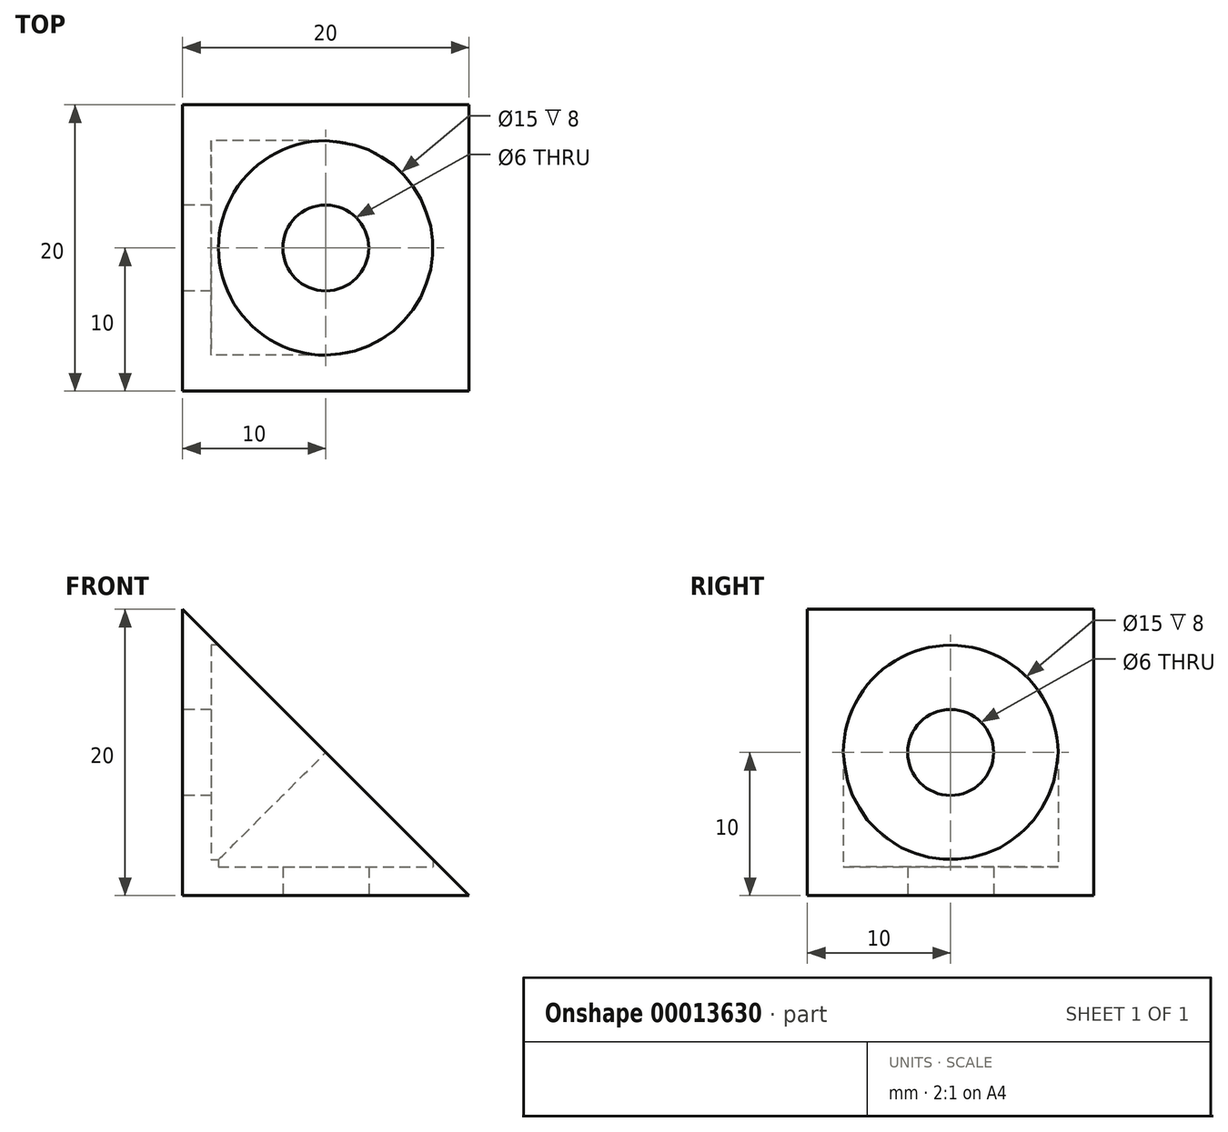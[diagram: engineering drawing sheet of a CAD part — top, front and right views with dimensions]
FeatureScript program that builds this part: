
annotation { "Feature Type Name" : "Feature", "Feature Type Description" : "" }
export const myFeature = defineFeature(function(context is Context, id is Id, definition is map)
    precondition{}
    {
        {
            var Q0;
            Q0=qCreatedBy(makeId("Front.planeOp"),FACE);
            var sketch = newSketch(context, id + "F0", { "sketchPlane" : qUnion([Q0])});
            skLineSegment(sketch, "E0", {"start": v(0, 0) * mm, "end": v(0, 20) * mm});
            skLineSegment(sketch, "E1", {"start": v(0, 0) * mm, "end": v(20, 0) * mm});
            skLineSegment(sketch, "E2", {"start": v(0, 20) * mm, "end": v(20, 0) * mm});
            skSolve(sketch);
        }
        {
            var Q0;
            Q0=makeQuery(id+"F0.imprint","IMPRINT",FACE,{"disambiguationData":[TD([[makeQuery(id+"F0.imprint","IMPRINT",EDGE,{"derivedFrom":sQuery(id+"F0.wireOp",EDGE,"E0")}),-1.0]])]});
            extrude(context, id + "F1", {"entities" : qUnion([Q0]), "depth" : 20 * mm});
        }
        {
            var Q0;
            Q0=makeQuery(id+"F1.opExtrude","SWEPT_FACE",FACE,{"disambiguationData":[OSD([sQuery(id+"F0.wireOp",EDGE,"E0")])]});
            var sketch = newSketch(context, id + "F2", { "sketchPlane" : qUnion([Q0])});
            skLineSegment(sketch, "E3", {"start": v(10, 0) * mm, "end": v(10, 20) * mm, "construction": true});
            skCircle(sketch, "E4", {"center": v(10, 10) * mm, "radius": 3 * mm});
            skCircle(sketch, "E5", {"center": v(10, 10) * mm, "radius": 7.5 * mm});
            skSolve(sketch);
        }
        {
            var Q0;
            Q0=makeQuery(id+"F2.imprint","IMPRINT",FACE,{"disambiguationData":[TD([[makeQuery(id+"F2.imprint","IMPRINT",EDGE,{"derivedFrom":sQuery(id+"F2.wireOp",EDGE,"E4")}),-1.0]])]});
            extrude(context, id + "F3", {"entities" : qUnion([Q0]), "operationType" : NewBodyOperationType.REMOVE, "oppositeDirection" : true, "depth" : 25 * mm});
        }
        {
            var Q0;
            Q0=makeQuery(id+"F2.imprint","IMPRINT",FACE,{"disambiguationData":[TD([[makeQuery(id+"F2.imprint","IMPRINT",EDGE,{"derivedFrom":sQuery(id+"F2.wireOp",EDGE,"E4")}),-1.0]])]});
            extrude(context, id + "F4", {"entities" : qUnion([Q0]), "operationType" : NewBodyOperationType.ADD, "oppositeDirection" : true, "depth" : 2 * mm});
        }
        {
            var Q0;
            Q0=makeQuery(id+"F2.imprint","IMPRINT",FACE,{"disambiguationData":[TD([[makeQuery(id+"F2.imprint","IMPRINT",EDGE,{"derivedFrom":sQuery(id+"F2.wireOp",EDGE,"E4")}),1.0]])]});
            extrude(context, id + "F5", {"entities" : qUnion([Q0]), "operationType" : NewBodyOperationType.REMOVE, "oppositeDirection" : true, "depth" : 25 * mm});
        }
        {
            var Q0;
            Q0=makeQuery(id+"F1.opExtrude","SWEPT_FACE",FACE,{"disambiguationData":[OSD([sQuery(id+"F0.wireOp",EDGE,"E1")])]});
            var sketch = newSketch(context, id + "F6", { "sketchPlane" : qUnion([Q0])});
            skLineSegment(sketch, "E6", {"start": v(0, 10) * mm, "end": v(20, 10) * mm, "construction": true});
            skCircle(sketch, "E7", {"center": v(10, 10) * mm, "radius": 7.5 * mm});
            skCircle(sketch, "E8", {"center": v(10, 10) * mm, "radius": 3 * mm});
            skSolve(sketch);
        }
        {
            var Q0;
            Q0=makeQuery(id+"F6.imprint","IMPRINT",FACE,{"disambiguationData":[TD([[makeQuery(id+"F6.imprint","IMPRINT",EDGE,{"derivedFrom":sQuery(id+"F6.wireOp",EDGE,"E7")}),1.0]])]});
            extrude(context, id + "F7", {"entities" : qUnion([Q0]), "operationType" : NewBodyOperationType.REMOVE, "oppositeDirection" : true, "depth" : 25 * mm});
        }
        {
            var Q0;
            Q0=makeQuery(id+"F6.imprint","IMPRINT",FACE,{"disambiguationData":[TD([[makeQuery(id+"F6.imprint","IMPRINT",EDGE,{"derivedFrom":sQuery(id+"F6.wireOp",EDGE,"E7")}),1.0]])]});
            extrude(context, id + "F8", {"entities" : qUnion([Q0]), "operationType" : NewBodyOperationType.ADD, "oppositeDirection" : true, "depth" : 2 * mm});
        }
        {
            var Q0;
            Q0=makeQuery(id+"F6.imprint","IMPRINT",FACE,{"disambiguationData":[TD([[makeQuery(id+"F6.imprint","IMPRINT",EDGE,{"derivedFrom":sQuery(id+"F6.wireOp",EDGE,"E8")}),1.0]])]});
            extrude(context, id + "F9", {"entities" : qUnion([Q0]), "operationType" : NewBodyOperationType.REMOVE, "oppositeDirection" : true, "depth" : 25 * mm});
        }
    });
